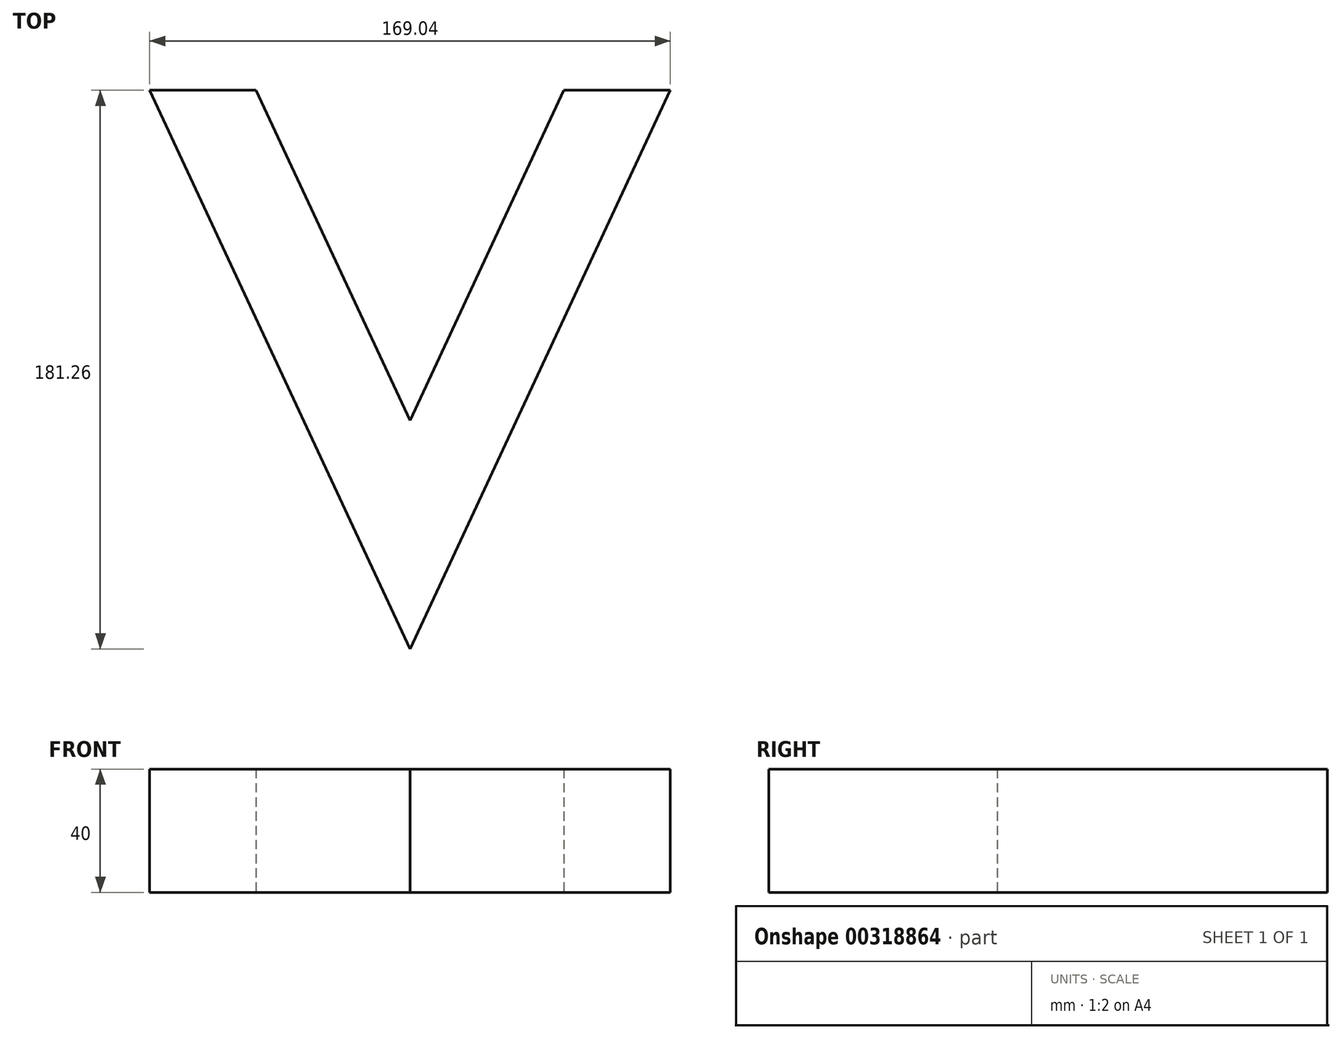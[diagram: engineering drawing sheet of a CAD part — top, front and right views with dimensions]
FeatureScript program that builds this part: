
annotation { "Feature Type Name" : "Feature", "Feature Type Description" : "" }
export const myFeature = defineFeature(function(context is Context, id is Id, definition is map)
    precondition{}
    {
        {
            var Q0;
            Q0=qCreatedBy(makeId("Top.planeOp"),FACE);
            var sketch = newSketch(context, id + "F0", { "sketchPlane" : qUnion([Q0])});
            skLineSegment(sketch, "E0.top", {"start": v(-84.52, 107.17) * mm, "end": v(-49.97, 107.17) * mm});
            skLineSegment(sketch, "E1", {"start": v(-84.52, 107.17) * mm, "end": v(0, -74.1) * mm});
            skLineSegment(sketch, "E2", {"start": v(0, 0) * mm, "end": v(-49.97, 107.17) * mm});
            skLineSegment(sketch, "E3.MirrorCS", {"start": v(84.52, 107.17) * mm, "end": v(0, -74.1) * mm});
            skLineSegment(sketch, "E4.MirrorCS", {"start": v(0, 0) * mm, "end": v(49.97, 107.17) * mm});
            skLineSegment(sketch, "E5.MirrorCS", {"start": v(84.52, 107.17) * mm, "end": v(49.97, 107.17) * mm});
            skSolve(sketch);
        }
        {
            var Q0;
            Q0=makeQuery(id+"F0.imprint","IMPRINT",FACE,{"disambiguationData":[TD([[makeQuery(id+"F0.imprint","IMPRINT",EDGE,{"derivedFrom":sQuery(id+"F0.wireOp",EDGE,"E0.top")}),-1.0]])]});
            extrude(context, id + "F1", {"entities" : qUnion([Q0]), "depth" : 40 * mm});
        }
    });
